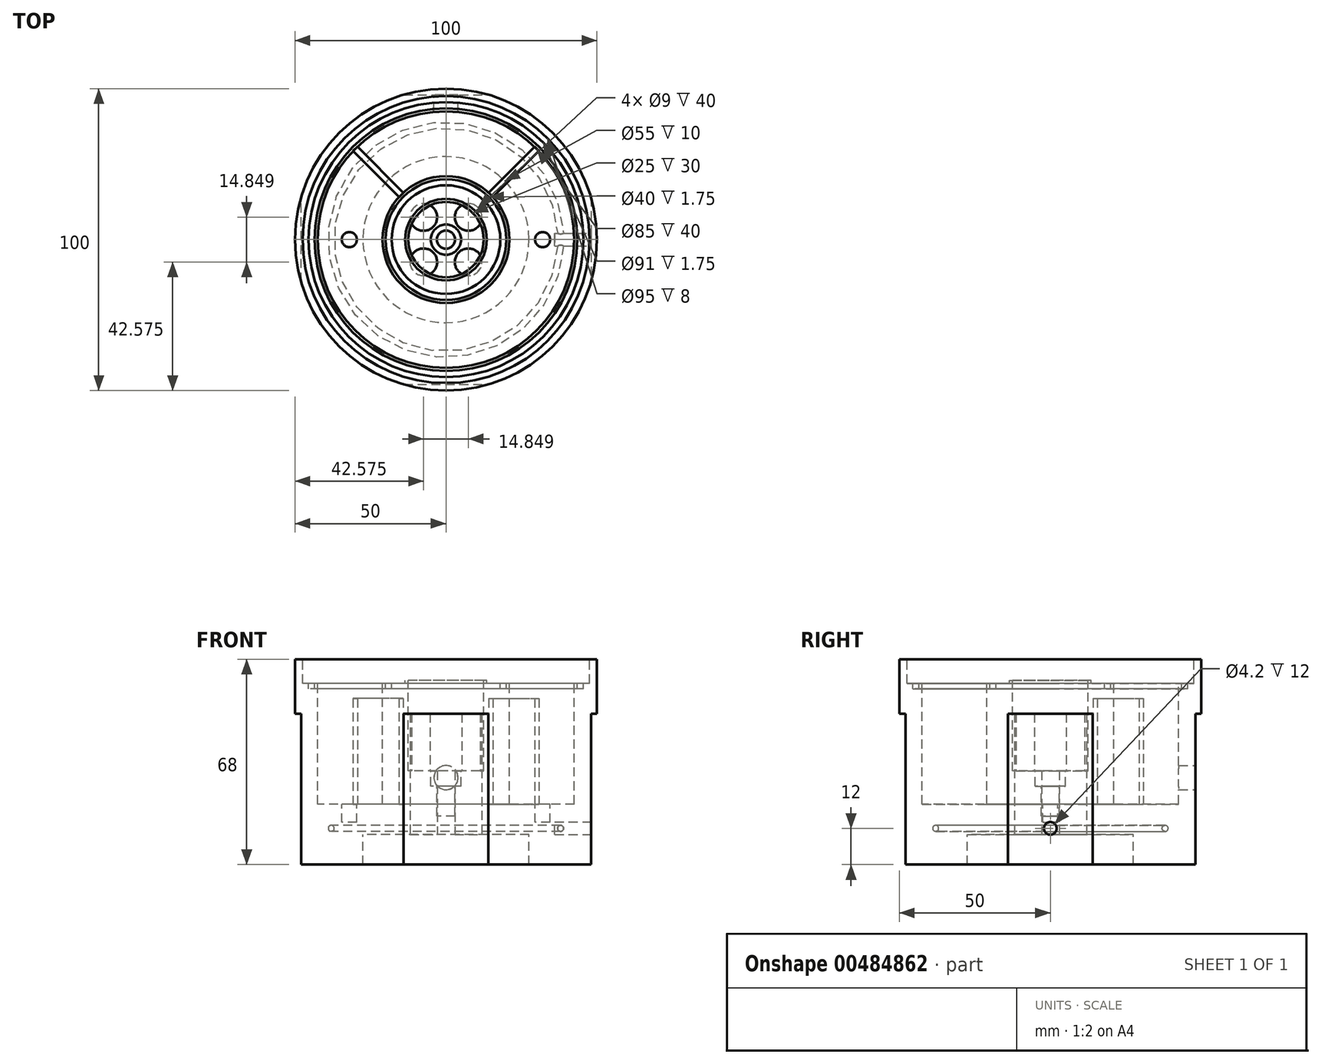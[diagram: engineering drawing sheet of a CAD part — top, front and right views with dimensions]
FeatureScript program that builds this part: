
annotation { "Feature Type Name" : "Feature", "Feature Type Description" : "" }
export const myFeature = defineFeature(function(context is Context, id is Id, definition is map)
    precondition{}
    {
        {
            var Q0;
            Q0=qCreatedBy(makeId("Front.planeOp"),FACE);
            var sketch = newSketch(context, id + "F0", { "sketchPlane" : qUnion([Q0])});
            skLineSegment(sketch, "E0", {"start": v(-50, 68) * mm, "end": v(-50, 0) * mm});
            skLineSegment(sketch, "E1", {"start": v(-50, 0) * mm, "end": v(-27.5, 0) * mm});
            skLineSegment(sketch, "E2", {"start": v(-42.5, 20) * mm, "end": v(-42.5, 60) * mm});
            skLineSegment(sketch, "E3", {"start": v(-47.5, 60) * mm, "end": v(-47.5, 68) * mm});
            skLineSegment(sketch, "E4", {"start": v(-47.5, 68) * mm, "end": v(-50, 68) * mm});
            skLineSegment(sketch, "E5", {"start": v(-12.5, 31) * mm, "end": v(-12.5, 60) * mm});
            skLineSegment(sketch, "E6", {"start": v(-42.5, 20) * mm, "end": v(-21, 20) * mm});
            skLineSegment(sketch, "E7", {"start": v(-12.5, 60) * mm, "end": v(-12.5, 61) * mm});
            skLineSegment(sketch, "E8", {"start": v(-12.5, 61) * mm, "end": v(-13.5, 61) * mm});
            skLineSegment(sketch, "E9", {"start": v(-13.5, 61) * mm, "end": v(-13.5, 60) * mm});
            skLineSegment(sketch, "E10", {"start": v(-45.5, 60) * mm, "end": v(-45.5, 58.25) * mm});
            skLineSegment(sketch, "E11", {"start": v(-45.5, 58.25) * mm, "end": v(-43.5, 58.25) * mm});
            skLineSegment(sketch, "E12", {"start": v(-43.5, 58.25) * mm, "end": v(-43.5, 60) * mm});
            skLineSegment(sketch, "E13", {"start": v(-47.5, 60) * mm, "end": v(-45.5, 60) * mm});
            skLineSegment(sketch, "E14", {"start": v(-43.5, 60) * mm, "end": v(-42.5, 60) * mm});
            skLineSegment(sketch, "E15", {"start": v(-3, 16) * mm, "end": v(0, 16) * mm});
            skLineSegment(sketch, "E16", {"start": v(0, 16) * mm, "end": v(0, 10) * mm});
            skLineSegment(sketch, "E17", {"start": v(-5, 31) * mm, "end": v(-5, 26) * mm});
            skLineSegment(sketch, "E18", {"start": v(-5, 26) * mm, "end": v(-3, 26) * mm});
            skLineSegment(sketch, "E19", {"start": v(-12.5, 31) * mm, "end": v(-5, 31) * mm});
            skLineSegment(sketch, "E20", {"start": v(-3, 26) * mm, "end": v(-3, 16) * mm});
            skLineSegment(sketch, "E21", {"start": v(0, 80.83) * mm, "end": v(0, -26.06) * mm, "construction": true});
            skCircle(sketch, "E22", {"center": v(-38, 12) * mm, "radius": 1 * mm});
            skLineSegment(sketch, "E23", {"start": v(-27.5, 10) * mm, "end": v(-27.5, 0) * mm});
            skLineSegment(sketch, "E24", {"start": v(-27.5, 10) * mm, "end": v(0, 10) * mm});
            skLineSegment(sketch, "E25", {"start": v(-21, 20) * mm, "end": v(-21, 60) * mm});
            skLineSegment(sketch, "E26", {"start": v(-21, 60) * mm, "end": v(-20, 60) * mm});
            skLineSegment(sketch, "E27", {"start": v(-20, 60) * mm, "end": v(-20, 58.25) * mm});
            skLineSegment(sketch, "E28", {"start": v(-20, 58.25) * mm, "end": v(-18, 58.25) * mm});
            skLineSegment(sketch, "E29", {"start": v(-18, 58.25) * mm, "end": v(-18, 60) * mm});
            skLineSegment(sketch, "E30", {"start": v(-18, 60) * mm, "end": v(-13.5, 60) * mm});
            skSolve(sketch);
        }
        {
            var Q0;
            Q0=makeQuery(id+"F0.imprint","IMPRINT",FACE,{"disambiguationData":[TD([[makeQuery(id+"F0.imprint","IMPRINT",EDGE,{"derivedFrom":sQuery(id+"F0.wireOp",EDGE,"E0")}),1.0]])]});
            var Q1;
            Q1=sQuery(id+"F0.wireOp",EDGE,"E21");
            revolve(context, id + "F1", {"entities" : qUnion([Q0]), "axis" : qUnion([Q1]), "revolveType" : RevolveType.FULL});
        }
        {
            var Q0;
            Q0=qCreatedBy(makeId("Front.planeOp"),FACE);
            var sketch = newSketch(context, id + "F2", { "sketchPlane" : qUnion([Q0])});
            skLineSegment(sketch, "E31.bottom", {"start": v(-92.1, -93.16) * mm, "end": v(-48, -93.16) * mm});
            skLineSegment(sketch, "E31.top", {"start": v(-92.1, 50) * mm, "end": v(-48, 50) * mm});
            skLineSegment(sketch, "E31.left", {"start": v(-92.1, -93.16) * mm, "end": v(-92.1, 50) * mm});
            skLineSegment(sketch, "E31.right", {"start": v(-48, -93.16) * mm, "end": v(-48, 50) * mm});
            skLineSegment(sketch, "E32.bottom", {"start": v(77.26, 50) * mm, "end": v(48, 50) * mm});
            skLineSegment(sketch, "E32.top", {"start": v(77.26, -108.46) * mm, "end": v(48, -108.46) * mm});
            skLineSegment(sketch, "E32.left", {"start": v(77.26, 50) * mm, "end": v(77.26, -108.46) * mm});
            skLineSegment(sketch, "E32.right", {"start": v(48, 50) * mm, "end": v(48, -108.46) * mm});
            skSolve(sketch);
        }
        {
            var Q0;
            Q0 = qSketchRegion(id + "F2", true);
            extrude(context, id + "F3", {"entities" : qUnion([Q0]), "operationType" : NewBodyOperationType.REMOVE, "endBound" : BoundingType.THROUGH_ALL, "depth" : 25 * mm, "hasSecondDirection" : true, "secondDirectionBound" : SecondDirectionBoundingType.THROUGH_ALL, "secondDirectionOppositeDirection" : true, "secondDirectionDepth" : 25 * mm});
        }
        {
            var Q0;
            Q0=makeQuery(id+"F3.boolean.opBoolean","COPY",FACE,{"derivedFrom":makeQuery(id+"F3.opExtrude","SWEPT_FACE",FACE,{"disambiguationData":[OSD([sQuery(id+"F2.wireOp",EDGE,"E32.right")])]})});
            var sketch = newSketch(context, id + "F4", { "sketchPlane" : qUnion([Q0])});
            skCircle(sketch, "E33", {"center": v(0, 12) * mm, "radius": 2.1 * mm});
            skSolve(sketch);
        }
        {
            var Q0;
            Q0 = qSketchRegion(id + "F4", true);
            extrude(context, id + "F5", {"entities" : qUnion([Q0]), "operationType" : NewBodyOperationType.REMOVE, "oppositeDirection" : true, "depth" : 12 * mm});
        }
        {
            var Q0;
            Q0=makeQuery(id+"F1.opRevolve","SWEPT_FACE",FACE,{"disambiguationData":[OSD([sQuery(id+"F0.wireOp",EDGE,"E24")])]});
            var sketch = newSketch(context, id + "F6", { "sketchPlane" : qUnion([Q0])});
            skCircle(sketch, "E34", {"center": v(0, 0) * mm, "radius": 10.5 * mm, "construction": true});
            skLineSegment(sketch, "E35", {"start": v(0, 0) * mm, "end": v(30, 30) * mm, "construction": true});
            skCircle(sketch, "E36", {"center": v(7.42, 7.42) * mm, "radius": 4.5 * mm});
            skCircle(sketch, "E37.1.0", {"center": v(-7.42, 7.42) * mm, "radius": 4.5 * mm});
            skCircle(sketch, "E37.2.0", {"center": v(-7.42, -7.42) * mm, "radius": 4.5 * mm});
            skCircle(sketch, "E37.3.0", {"center": v(7.42, -7.42) * mm, "radius": 4.5 * mm});
            skSolve(sketch);
        }
        {
            var Q0;
            Q0 = qSketchRegion(id + "F6", true);
            extrude(context, id + "F7", {"entities" : qUnion([Q0]), "operationType" : NewBodyOperationType.REMOVE, "oppositeDirection" : true, "depth" : 40 * mm});
        }
        {
            var Q0;
            Q0=makeQuery(id+"F1.opRevolve","SWEPT_FACE",FACE,{"disambiguationData":[OSD([sQuery(id+"F0.wireOp",EDGE,"E6")])]});
            var sketch = newSketch(context, id + "F8", { "sketchPlane" : qUnion([Q0])});
            skCircle(sketch, "E38", {"center": v(0, 0) * mm, "radius": 32 * mm, "construction": true});
            skCircle(sketch, "E39", {"center": v(-32, 0) * mm, "radius": 2.5 * mm});
            skCircle(sketch, "E40", {"center": v(32, 0) * mm, "radius": 2.5 * mm});
            skSolve(sketch);
        }
        {
            var Q0;
            Q0 = qSketchRegion(id + "F8", true);
            extrude(context, id + "F9", {"entities" : qUnion([Q0]), "operationType" : NewBodyOperationType.REMOVE, "oppositeDirection" : true, "depth" : 6 * mm});
        }
        {
            var Q0;
            Q0=makeQuery(id+"F1.opRevolve","SWEPT_FACE",FACE,{"disambiguationData":[OSD([sQuery(id+"F0.wireOp",EDGE,"E6")])]});
            var sketch = newSketch(context, id + "F10", { "sketchPlane" : qUnion([Q0])});
            skLineSegment(sketch, "E41", {"start": v(0, 0) * mm, "end": v(-43.07, 43.07) * mm, "construction": true});
            skLineSegment(sketch, "E42", {"start": v(0, 0) * mm, "end": v(45.06, 45.06) * mm, "construction": true});
            skLineSegment(sketch, "E43", {"start": v(14.13, 15.54) * mm, "end": v(29.34, 30.75) * mm});
            skLineSegment(sketch, "E44", {"start": v(15.54, 14.13) * mm, "end": v(30.75, 29.34) * mm});
            skLineSegment(sketch, "E45", {"start": v(-14.13, 15.54) * mm, "end": v(-29.34, 30.75) * mm});
            skLineSegment(sketch, "E46", {"start": v(-15.54, 14.13) * mm, "end": v(-30.75, 29.34) * mm});
            skLineSegment(sketch, "E47", {"start": v(29.34, 30.75) * mm, "end": v(30.75, 29.34) * mm});
            skLineSegment(sketch, "E48", {"start": v(14.13, 15.54) * mm, "end": v(15.54, 14.13) * mm});
            skLineSegment(sketch, "E49", {"start": v(-15.54, 14.13) * mm, "end": v(-14.13, 15.54) * mm});
            skLineSegment(sketch, "E50", {"start": v(-30.75, 29.34) * mm, "end": v(-29.34, 30.75) * mm});
            skSolve(sketch);
        }
        {
            var Q0;
            Q0 = qSketchRegion(id + "F10", true);
            extrude(context, id + "F11", {"entities" : qUnion([Q0]), "depth" : 35 * mm});
        }
        {
            var Q0;
            Q0=qCreatedBy(makeId("Right.planeOp"),FACE);
            var sketch = newSketch(context, id + "F12", { "sketchPlane" : qUnion([Q0])});
            skLineSegment(sketch, "E51.bottom", {"start": v(92.55, -19.6) * mm, "end": v(48, -19.6) * mm});
            skLineSegment(sketch, "E51.top", {"start": v(92.55, 50) * mm, "end": v(48, 50) * mm});
            skLineSegment(sketch, "E51.left", {"start": v(92.55, -19.6) * mm, "end": v(92.55, 50) * mm});
            skLineSegment(sketch, "E51.right", {"start": v(48, -19.6) * mm, "end": v(48, 50) * mm});
            skLineSegment(sketch, "E52.bottom", {"start": v(-85.23, -32.51) * mm, "end": v(-48, -32.51) * mm});
            skLineSegment(sketch, "E52.top", {"start": v(-85.23, 50) * mm, "end": v(-48, 50) * mm});
            skLineSegment(sketch, "E52.left", {"start": v(-85.23, -32.51) * mm, "end": v(-85.23, 50) * mm});
            skLineSegment(sketch, "E52.right", {"start": v(-48, -32.51) * mm, "end": v(-48, 50) * mm});
            skSolve(sketch);
        }
        {
            var Q0;
            Q0 = qSketchRegion(id + "F12", true);
            extrude(context, id + "F13", {"entities" : qUnion([Q0]), "operationType" : NewBodyOperationType.REMOVE, "endBound" : BoundingType.THROUGH_ALL, "oppositeDirection" : true, "depth" : 25 * mm, "hasSecondDirection" : true, "secondDirectionBound" : SecondDirectionBoundingType.THROUGH_ALL, "secondDirectionOppositeDirection" : false, "secondDirectionDepth" : 25 * mm});
        }
        {
            var Q0;
            Q0=makeQuery(id+"F13.boolean.opBoolean","COPY",FACE,{"derivedFrom":makeQuery(id+"F13.opExtrude","SWEPT_FACE",FACE,{"disambiguationData":[OSD([sQuery(id+"F12.wireOp",EDGE,"E51.right")])]})});
            var sketch = newSketch(context, id + "F14", { "sketchPlane" : qUnion([Q0])});
            skCircle(sketch, "E53", {"center": v(0, 28.81) * mm, "radius": 4 * mm});
            skSolve(sketch);
        }
        {
            var Q0;
            Q0 = qSketchRegion(id + "F14", true);
            extrude(context, id + "F15", {"entities" : qUnion([Q0]), "operationType" : NewBodyOperationType.REMOVE, "oppositeDirection" : true, "depth" : 10 * mm});
        }
    });
